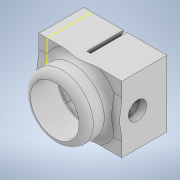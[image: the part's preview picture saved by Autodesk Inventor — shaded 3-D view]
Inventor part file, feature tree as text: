
AUTODESK INVENTOR PART (.ipt)
format: ipt  version: 2020 (Build 240168000, 168)  size: 304,128 bytes
history: native  units: mm
features: sketch x14, extrude x11, projected_geometry x9, other x3, fillet x2, chamfer x2
ambient origin geometry x8: Origin, YZ Plane, XZ Plane, XY Plane, X Axis, Y Axis, Z Axis, Center Point
bodies: Solid1 (feature_tree)
feature tree (41):
  other  "camera and mount block.iam"
  other  "camera mount block.ipt:1"
  other  "dummy camera.ipt:1"
  extrude  "Extrusion1"  Depth=10.0mm TaperAngle=0.0deg
  extrude  "Extrusion2"  Depth=10.0mm
  extrude  "Extrusion3"  Depth=2.0mm TaperAngle=0.0deg
  sketch  "Sketch6"  dims[d13=0.1mm d14=7.0mm d15=0.0mm]
  extrude  "Extrusion4"  Depth=7.0mm TaperAngle=0.0deg
  extrude  "Extrusion5"  Depth=7.0mm TaperAngle=0.0deg
  extrude  "Extrusion6"  Depth=2.0mm
  fillet  "Fillet1"  Radius=2.2mm
  fillet  "Fillet2"  Radius=2.2mm
  chamfer  "Chamfer2"  Distance=2.0mm
  sketch  "Sketch10"  dims[d31=5.0mm d32=2.0mm d33=0.0mm]
  sketch  "Sketch11"  dims[d34=1.5mm d35=2.0mm d36=45.0deg d37=0.5mm]
  extrude  "Extrusion7"  Depth=2.0mm TaperAngle=0.0deg
  extrude  "Extrusion8"  Depth=0.5mm
  extrude  "Extrusion9"  Depth=10.0mm TaperAngle=0.0deg
  extrude  "Extrusion10"  [1 undecoded]
  chamfer  "Chamfer3"  [1 undecoded]
  extrude  "Extrusion11"  [1 undecoded]
  sketch  "Sketch1"  dims[d0=10.0mm d1=10.0mm d2=0.0mm]
  sketch  "Sketch9"  dims[d28=5.0mm d29=2.0mm d30=0.0mm]
  sketch  "Sketch3"  dims[d3=10.0mm d4=0.0mm d5=2.0mm]
  projected_geometry  "Projected Loop1"
  sketch  "Sketch4"  dims[d6=7.0mm d7=0.0mm d8=2.0mm d9=0.0mm]
  projected_geometry  "Projected Loop2"
  sketch  "Sketch5"  dims[d10=0.2mm d11=7.0mm d12=0.0mm]
  projected_geometry  "Projected Loop3"
  sketch  "Sketch7"  dims[d16=2.0mm d17=2.0mm]
  projected_geometry  "Projected Loop4"
  sketch  "Sketch8"  dims[d21=1.0mm d22=2.0mm d23=45.0deg d24=2.2mm d25=0.0mm d26=2.2mm d27=0.0mm]
  projected_geometry  "Projected Loop5"
  projected_geometry  "Projected Loop6"
  projected_geometry  "Projected Loop7"
  sketch  "Sketch12"  dims[d38=0.5mm d39=10.0mm d40=0.0mm]
  projected_geometry  "Projected Loop8"
  sketch  "Sketch13"
  sketch  "Sketch14"
  sketch  "Sketch15"
  projected_geometry  "Projected Loop9"
note: 3 required parameter values undecoded (feature->parameter linkage not recoverable at this tier; creation-order binding heuristic only, values carry confidence <= 0.55)
